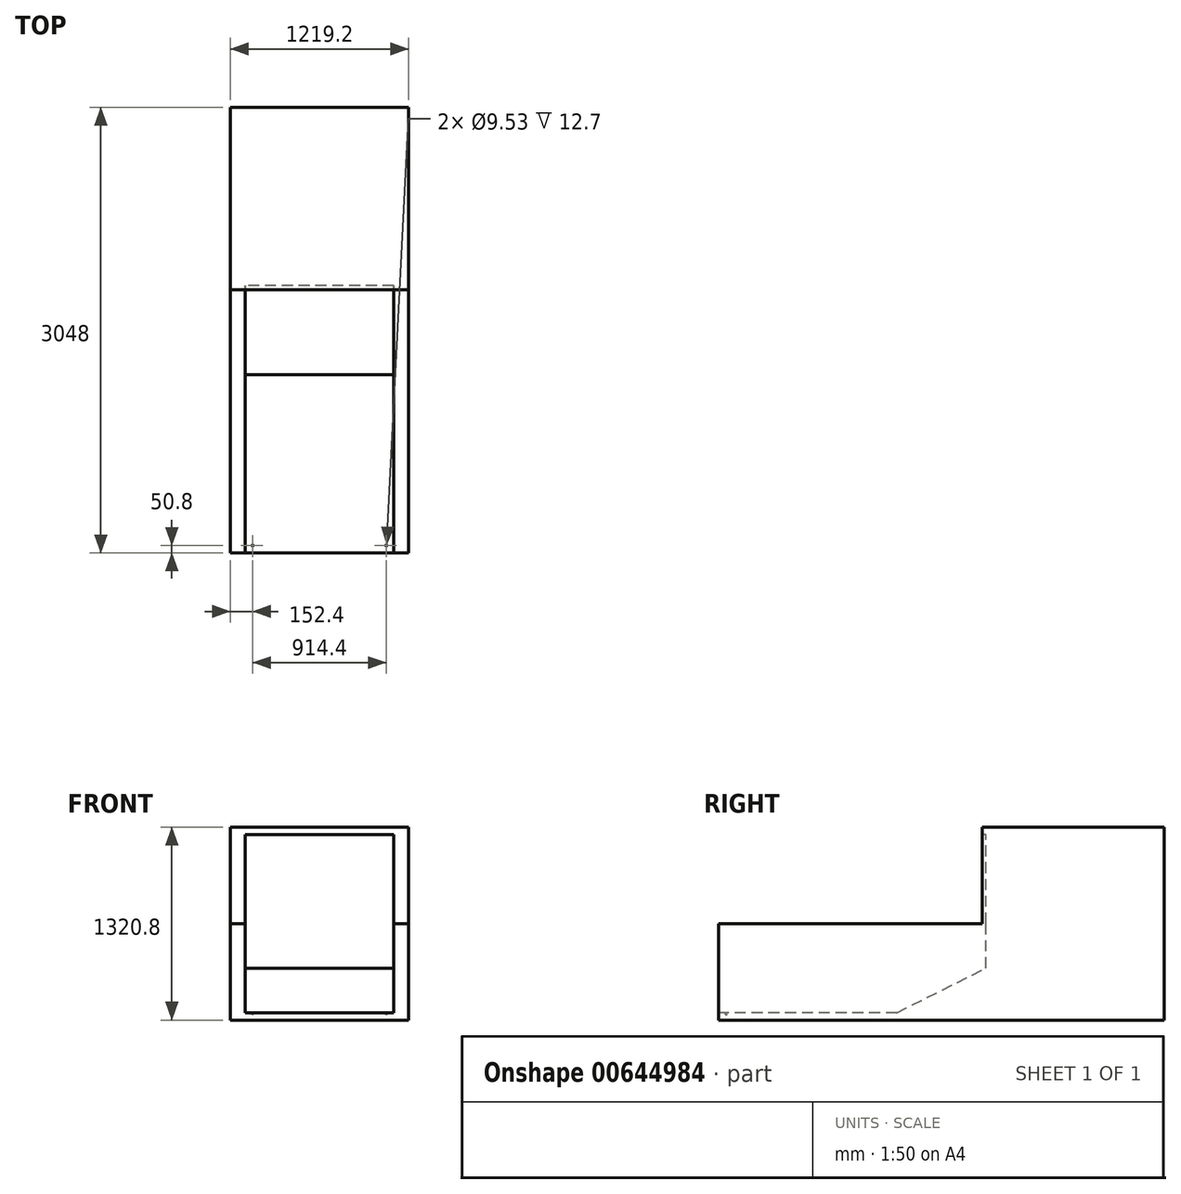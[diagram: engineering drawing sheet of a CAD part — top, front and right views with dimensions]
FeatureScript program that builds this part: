
annotation { "Feature Type Name" : "Feature", "Feature Type Description" : "" }
export const myFeature = defineFeature(function(context is Context, id is Id, definition is map)
    precondition{}
    {
        {
            var Q0;
            Q0=qCreatedBy(makeId("Front.planeOp"),FACE);
            var sketch = newSketch(context, id + "F0", { "sketchPlane" : qUnion([Q0])});
            skLineSegment(sketch, "E0.bottom", {"start": v(609.6, 660.4) * mm, "end": v(-609.6, 660.4) * mm});
            skLineSegment(sketch, "E0.top", {"start": v(609.6, -660.4) * mm, "end": v(-609.6, -660.4) * mm});
            skLineSegment(sketch, "E0.left", {"start": v(609.6, 660.4) * mm, "end": v(609.6, -660.4) * mm});
            skLineSegment(sketch, "E0.right", {"start": v(-609.6, 660.4) * mm, "end": v(-609.6, -660.4) * mm});
            skPoint(sketch, "E0.middle", {"position": v(0, 0) * mm});
            skSolve(sketch);
        }
        {
            var Q0;
            Q0=makeQuery(id+"F0.imprint","IMPRINT",FACE,{"disambiguationData":[TD([[makeQuery(id+"F0.imprint","IMPRINT",EDGE,{"derivedFrom":sQuery(id+"F0.wireOp",EDGE,"E0.bottom")}),1.0]])]});
            extrude(context, id + "F1", {"entities" : qUnion([Q0]), "oppositeDirection" : true, "depth" : 3048 * mm, "offsetDistance" : 25.4 * mm});
        }
        {
            var Q0;
            Q0=makeQuery(id+"F1.opExtrude","CAP_FACE",FACE,{"disambiguationData":[OSD([sQuery(id+"F0.wireOp",EDGE,"E0.bottom"),sQuery(id+"F0.wireOp",EDGE,"E0.top"),sQuery(id+"F0.wireOp",EDGE,"E0.left"),sQuery(id+"F0.wireOp",EDGE,"E0.right")])],"isStart":true});
            var sketch = newSketch(context, id + "F2", { "sketchPlane" : qUnion([Q0])});
            skLineSegment(sketch, "E1.bottom", {"start": v(508, 609.6) * mm, "end": v(-508, 609.6) * mm});
            skLineSegment(sketch, "E1.top", {"start": v(508, -609.6) * mm, "end": v(-508, -609.6) * mm});
            skLineSegment(sketch, "E1.left", {"start": v(508, 609.6) * mm, "end": v(508, -609.6) * mm});
            skLineSegment(sketch, "E1.right", {"start": v(-508, 609.6) * mm, "end": v(-508, -609.6) * mm});
            skPoint(sketch, "E1.middle", {"position": v(0, 0) * mm});
            skSolve(sketch);
        }
        {
            var Q0;
            Q0=makeQuery(id+"F2.imprint","IMPRINT",FACE,{"disambiguationData":[TD([[makeQuery(id+"F2.imprint","IMPRINT",EDGE,{"derivedFrom":sQuery(id+"F2.wireOp",EDGE,"E1.bottom")}),1.0]])]});
            extrude(context, id + "F3", {"entities" : qUnion([Q0]), "operationType" : NewBodyOperationType.REMOVE, "oppositeDirection" : true, "depth" : 1219.2 * mm, "offsetDistance" : 25.4 * mm});
        }
        {
            var Q0;
            Q0=makeQuery(id+"F3.boolean.opBoolean","COPY",FACE,{"derivedFrom":makeQuery(id+"F3.opExtrude","CAP_FACE",FACE,{"disambiguationData":[OSD([sQuery(id+"F2.wireOp",EDGE,"E1.bottom"),sQuery(id+"F2.wireOp",EDGE,"E1.top"),sQuery(id+"F2.wireOp",EDGE,"E1.left"),sQuery(id+"F2.wireOp",EDGE,"E1.right")])],"isStart":false})});
            var sketch = newSketch(context, id + "F4", { "sketchPlane" : qUnion([Q0])});
            skLineSegment(sketch, "E2.bottom", {"start": v(508, 609.6) * mm, "end": v(-508, 609.6) * mm});
            skLineSegment(sketch, "E2.top", {"start": v(508, -304.8) * mm, "end": v(-508, -304.8) * mm});
            skLineSegment(sketch, "E2.left", {"start": v(508, 609.6) * mm, "end": v(508, -304.8) * mm});
            skLineSegment(sketch, "E2.right", {"start": v(-508, 609.6) * mm, "end": v(-508, -304.8) * mm});
            skSolve(sketch);
        }
        {
            var Q0;
            Q0=makeQuery(id+"F4.imprint","IMPRINT",FACE,{"disambiguationData":[TD([[makeQuery(id+"F4.imprint","IMPRINT",EDGE,{"derivedFrom":sQuery(id+"F4.wireOp",EDGE,"E2.bottom")}),1.0]])]});
            extrude(context, id + "F5", {"entities" : qUnion([Q0]), "operationType" : NewBodyOperationType.REMOVE, "oppositeDirection" : true, "depth" : 609.6 * mm, "offsetDistance" : 25.4 * mm});
        }
        {
            var Q0;
            Q0=makeQuery(id+"F5.boolean.opBoolean","MERGE",FACE,{"derivedFrom":[makeQuery(id+"F3.boolean.opBoolean","COPY",FACE,{"derivedFrom":makeQuery(id+"F3.opExtrude","SWEPT_FACE",FACE,{"disambiguationData":[OSD([sQuery(id+"F2.wireOp",EDGE,"E1.right")])]})}),makeQuery(id+"F5.opExtrude","SWEPT_FACE",FACE,{"disambiguationData":[OSD([sQuery(id+"F4.wireOp",EDGE,"E2.right")])]})]});
            var Q1;
            Q1=makeQuery(id+"F5.boolean.opBoolean","MERGE",FACE,{"derivedFrom":[makeQuery(id+"F3.boolean.opBoolean","COPY",FACE,{"derivedFrom":makeQuery(id+"F3.opExtrude","SWEPT_FACE",FACE,{"disambiguationData":[OSD([sQuery(id+"F2.wireOp",EDGE,"E1.left")])]})}),makeQuery(id+"F5.opExtrude","SWEPT_FACE",FACE,{"disambiguationData":[OSD([sQuery(id+"F4.wireOp",EDGE,"E2.left")])]})]});
            cPlane(context, id + "F6", {"entities" : qUnion([Q0, Q1]), "cplaneType" : CPlaneType.MID_PLANE, "offset" : 25.4 * mm, "width" : 152.4 * mm, "height" : 152.4 * mm});
        }
        {
            var Q0;
            Q0=qCreatedBy(id+"F6.planeOp",FACE);
            var sketch = newSketch(context, id + "F7", { "sketchPlane" : qUnion([Q0])});
            skLineSegment(sketch, "E3", {"start": v(0, 0) * mm, "end": v(0, -609.6) * mm});
            skLineSegment(sketch, "E4", {"start": v(0, -609.6) * mm, "end": v(1219.2, -609.6) * mm});
            skLineSegment(sketch, "E5", {"start": v(1219.2, -609.6) * mm, "end": v(1828.8, -304.8) * mm});
            skLineSegment(sketch, "E6", {"start": v(1828.8, -304.8) * mm, "end": v(1828.8, 0) * mm});
            skLineSegment(sketch, "E7", {"start": v(1828.8, 0) * mm, "end": v(0, 0) * mm});
            skSolve(sketch);
        }
        {
            var Q0;
            Q0=makeQuery(id+"F7.imprint","IMPRINT",FACE,{"disambiguationData":[TD([[makeQuery(id+"F7.imprint","IMPRINT",EDGE,{"derivedFrom":sQuery(id+"F7.wireOp",EDGE,"E3")}),1.0]])]});
            extrude(context, id + "F8", {"entities" : qUnion([Q0]), "operationType" : NewBodyOperationType.REMOVE, "oppositeDirection" : true, "depth" : 508 * mm, "offsetDistance" : 25.4 * mm, "hasSecondDirection" : true, "secondDirectionOppositeDirection" : false, "secondDirectionDepth" : 508 * mm});
        }
        {
            var Q0;
            Q0=makeQuery(id+"F1.opExtrude","CAP_FACE",FACE,{"disambiguationData":[OSD([sQuery(id+"F0.wireOp",EDGE,"E0.bottom"),sQuery(id+"F0.wireOp",EDGE,"E0.top"),sQuery(id+"F0.wireOp",EDGE,"E0.left"),sQuery(id+"F0.wireOp",EDGE,"E0.right")])],"isStart":true});
            var sketch = newSketch(context, id + "F9", { "sketchPlane" : qUnion([Q0])});
            skLineSegment(sketch, "E8.bottom", {"start": v(-609.6, 660.4) * mm, "end": v(609.6, 660.4) * mm});
            skLineSegment(sketch, "E8.top", {"start": v(-609.6, 0) * mm, "end": v(609.6, 0) * mm});
            skLineSegment(sketch, "E8.left", {"start": v(-609.6, 660.4) * mm, "end": v(-609.6, 0) * mm});
            skLineSegment(sketch, "E8.right", {"start": v(609.6, 660.4) * mm, "end": v(609.6, 0) * mm});
            skSolve(sketch);
        }
        {
            var Q0;
            Q0 = qSketchRegion(id + "F9", true);
            extrude(context, id + "F10", {"entities" : qUnion([Q0]), "operationType" : NewBodyOperationType.REMOVE, "oppositeDirection" : true, "depth" : 1800.86 * mm, "offsetDistance" : 25.4 * mm});
        }
        {
            var Q0;
            Q0=makeQuery(id+"F3.boolean.opBoolean","COPY",FACE,{"derivedFrom":makeQuery(id+"F3.opExtrude","SWEPT_FACE",FACE,{"disambiguationData":[OSD([sQuery(id+"F2.wireOp",EDGE,"E1.top")])]})});
            var sketch = newSketch(context, id + "F11", { "sketchPlane" : qUnion([Q0])});
            skLineSegment(sketch, "E9.bottom", {"start": v(-508, 0) * mm, "end": v(-457.2, 0) * mm});
            skLineSegment(sketch, "E9.top", {"start": v(-508, 50.8) * mm, "end": v(-457.2, 50.8) * mm});
            skLineSegment(sketch, "E9.left", {"start": v(-508, 0) * mm, "end": v(-508, 50.8) * mm});
            skLineSegment(sketch, "E9.right", {"start": v(-457.2, 0) * mm, "end": v(-457.2, 50.8) * mm});
            skCircle(sketch, "E10", {"center": v(-457.2, 50.8) * mm, "radius": 4.76 * mm});
            skLineSegment(sketch, "E11.bottom", {"start": v(508, 0) * mm, "end": v(457.2, 0) * mm});
            skLineSegment(sketch, "E11.top", {"start": v(508, 50.8) * mm, "end": v(457.2, 50.8) * mm});
            skLineSegment(sketch, "E11.left", {"start": v(508, 0) * mm, "end": v(508, 50.8) * mm});
            skLineSegment(sketch, "E11.right", {"start": v(457.2, 0) * mm, "end": v(457.2, 50.8) * mm});
            skCircle(sketch, "E12", {"center": v(457.2, 50.8) * mm, "radius": 4.76 * mm});
            skSolve(sketch);
        }
        {
            var Q0;
            {var subQ0=sQuery(id+"F11.wireOp",EDGE,"E9.right");var subQ1=sQuery(id+"F11.wireOp",EDGE,"E9.top");var subQ2=makeQuery(id+"F11.imprint","INTERSECT",VERTEX,{"derivedFrom":[subQ1,subQ0]});Q0=makeQuery(id+"F11.imprint","IMPRINT",FACE,{"disambiguationData":[TD([[makeQuery(id+"F11.imprint","IMPRINT",EDGE,{"disambiguationData":[TD([[subQ2,1.0]])],"derivedFrom":subQ1}),1.0]])]});}
            var Q1;
            {var subQ0=sQuery(id+"F11.wireOp",EDGE,"E9.right");var subQ1=sQuery(id+"F11.wireOp",EDGE,"E9.top");var subQ2=makeQuery(id+"F11.imprint","INTERSECT",VERTEX,{"derivedFrom":[subQ1,subQ0]});Q1=makeQuery(id+"F11.imprint","IMPRINT",FACE,{"disambiguationData":[TD([[makeQuery(id+"F11.imprint","IMPRINT",EDGE,{"disambiguationData":[TD([[subQ2,1.0]])],"derivedFrom":subQ1}),-1.0]])]});}
            var Q2;
            {var subQ0=sQuery(id+"F11.wireOp",EDGE,"E11.right");var subQ1=sQuery(id+"F11.wireOp",EDGE,"E11.top");var subQ2=makeQuery(id+"F11.imprint","INTERSECT",VERTEX,{"derivedFrom":[subQ1,subQ0]});Q2=makeQuery(id+"F11.imprint","IMPRINT",FACE,{"disambiguationData":[TD([[makeQuery(id+"F11.imprint","IMPRINT",EDGE,{"disambiguationData":[TD([[subQ2,1.0]])],"derivedFrom":subQ1}),1.0]])]});}
            var Q3;
            {var subQ0=sQuery(id+"F11.wireOp",EDGE,"E11.right");var subQ1=sQuery(id+"F11.wireOp",EDGE,"E11.top");var subQ2=makeQuery(id+"F11.imprint","INTERSECT",VERTEX,{"derivedFrom":[subQ1,subQ0]});Q3=makeQuery(id+"F11.imprint","IMPRINT",FACE,{"disambiguationData":[TD([[makeQuery(id+"F11.imprint","IMPRINT",EDGE,{"disambiguationData":[TD([[subQ2,1.0]])],"derivedFrom":subQ1}),-1.0]])]});}
            extrude(context, id + "F12", {"entities" : qUnion([Q0, Q1, Q2, Q3]), "operationType" : NewBodyOperationType.REMOVE, "oppositeDirection" : true, "depth" : 12.7 * mm, "offsetDistance" : 25.4 * mm});
        }
    });
